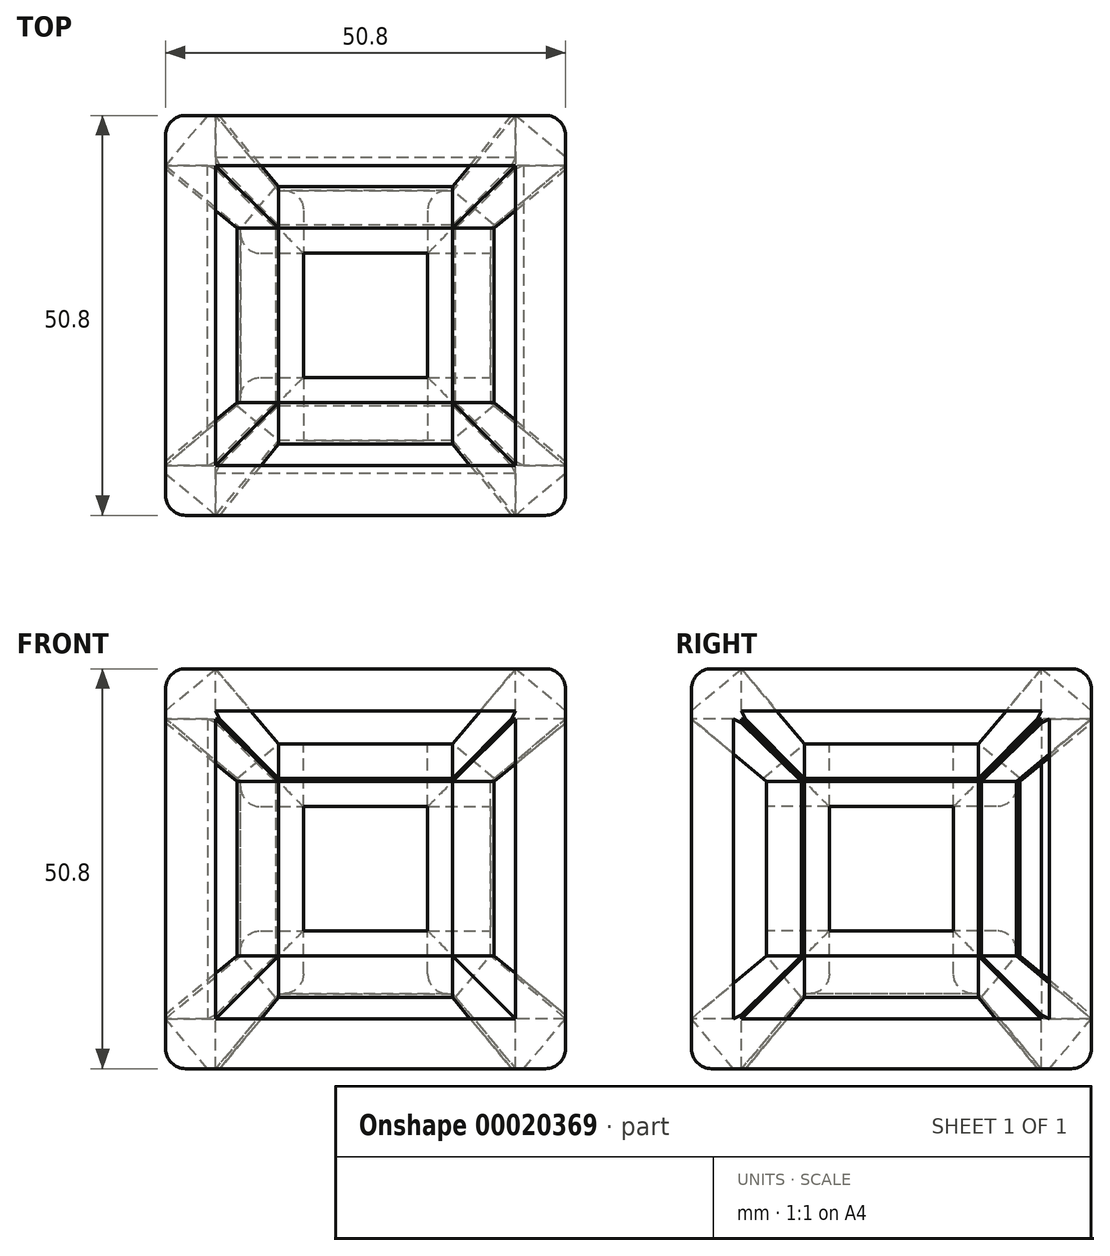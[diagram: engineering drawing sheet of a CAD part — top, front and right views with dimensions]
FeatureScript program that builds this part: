
annotation { "Feature Type Name" : "Feature", "Feature Type Description" : "" }
export const myFeature = defineFeature(function(context is Context, id is Id, definition is map)
    precondition{}
    {
        {
            var Q0;
            Q0=qCreatedBy(makeId("Front.planeOp"),FACE);
            var sketch = newSketch(context, id + "F0", { "sketchPlane" : qUnion([Q0])});
            skLineSegment(sketch, "E0.rect.bottom", {"start": v(-50.8, 50.8) * mm, "end": v(50.8, 50.8) * mm});
            skLineSegment(sketch, "E0.rect.top", {"start": v(-50.8, -50.8) * mm, "end": v(50.8, -50.8) * mm});
            skLineSegment(sketch, "E0.rect.left", {"start": v(-50.8, 50.8) * mm, "end": v(-50.8, -50.8) * mm});
            skLineSegment(sketch, "E0.rect.right", {"start": v(50.8, 50.8) * mm, "end": v(50.8, -50.8) * mm});
            skPoint(sketch, "E0.rect.middle", {"position": v(0, 0) * mm});
            skLineSegment(sketch, "E1.rect.bottom", {"start": v(-44.45, 44.45) * mm, "end": v(44.45, 44.45) * mm});
            skLineSegment(sketch, "E1.rect.top", {"start": v(-44.45, -44.45) * mm, "end": v(44.45, -44.45) * mm});
            skLineSegment(sketch, "E1.rect.left", {"start": v(-44.45, 44.45) * mm, "end": v(-44.45, -44.45) * mm});
            skLineSegment(sketch, "E1.rect.right", {"start": v(44.45, 44.45) * mm, "end": v(44.45, -44.45) * mm});
            skSolve(sketch);
        }
        {
            var Q0;
            Q0=makeQuery(id+"F0.imprint","IMPRINT",FACE,{"disambiguationData":[TD([[makeQuery(id+"F0.imprint","IMPRINT",EDGE,{"derivedFrom":sQuery(id+"F0.wireOp",EDGE,"E0.rect.bottom")}),-1.0]])]});
            var Q1;
            Q1=makeQuery(id+"F0.imprint","IMPRINT",FACE,{"disambiguationData":[TD([[makeQuery(id+"F0.imprint","IMPRINT",EDGE,{"derivedFrom":sQuery(id+"F0.wireOp",EDGE,"E1.rect.bottom")}),-1.0]])]});
            extrude(context, id + "F1", {"entities" : qUnion([Q0, Q1]), "oppositeDirection" : true, "depth" : 101.6 * mm});
        }
        {
            var Q0;
            Q0=makeQuery(id+"F1.opExtrude","CAP_FACE",FACE,{"disambiguationData":[OSD([sQuery(id+"F0.wireOp",EDGE,"E0.rect.bottom"),sQuery(id+"F0.wireOp",EDGE,"E0.rect.top"),sQuery(id+"F0.wireOp",EDGE,"E0.rect.left"),sQuery(id+"F0.wireOp",EDGE,"E0.rect.right")])],"isStart":true});
            var sketch = newSketch(context, id + "F2", { "sketchPlane" : qUnion([Q0])});
            skLineSegment(sketch, "E2.rect.bottom", {"start": v(-38.1, 38.1) * mm, "end": v(38.1, 38.1) * mm});
            skLineSegment(sketch, "E2.rect.top", {"start": v(-38.1, -38.1) * mm, "end": v(38.1, -38.1) * mm});
            skLineSegment(sketch, "E2.rect.left", {"start": v(-38.1, 38.1) * mm, "end": v(-38.1, -38.1) * mm});
            skLineSegment(sketch, "E2.rect.right", {"start": v(38.1, 38.1) * mm, "end": v(38.1, -38.1) * mm});
            skPoint(sketch, "E2.rect.middle", {"position": v(0, 0) * mm});
            skSolve(sketch);
        }
        {
            var Q0;
            Q0=makeQuery(id+"F2.imprint","IMPRINT",FACE,{"disambiguationData":[TD([[makeQuery(id+"F2.imprint","IMPRINT",EDGE,{"derivedFrom":sQuery(id+"F2.wireOp",EDGE,"E2.rect.bottom")}),-1.0]])]});
            extrude(context, id + "F3", {"entities" : qUnion([Q0]), "operationType" : NewBodyOperationType.REMOVE, "oppositeDirection" : true, "depth" : 19.05 * mm, "hasDraft" : true, "draftAngle" : 40 * degree, "draftPullDirection" : true});
        }
        {
            var Q0;
            Q0=makeQuery(id+"F1.opExtrude","SWEPT_FACE",FACE,{"disambiguationData":[OSD([sQuery(id+"F0.wireOp",EDGE,"E0.rect.right")])]});
            var sketch = newSketch(context, id + "F4", { "sketchPlane" : qUnion([Q0])});
            skLineSegment(sketch, "E3.rect.bottom", {"start": v(12.7, 38.1) * mm, "end": v(88.9, 38.1) * mm});
            skLineSegment(sketch, "E3.rect.top", {"start": v(12.7, -38.1) * mm, "end": v(88.9, -38.1) * mm});
            skLineSegment(sketch, "E3.rect.left", {"start": v(12.7, 38.1) * mm, "end": v(12.7, -38.1) * mm});
            skLineSegment(sketch, "E3.rect.right", {"start": v(88.9, 38.1) * mm, "end": v(88.9, -38.1) * mm});
            skPoint(sketch, "E3.rect.middle", {"position": v(50.8, 0) * mm});
            skPoint(sketch, "E4.start.orphan", {"position": v(0, 50.8) * mm});
            skPoint(sketch, "E5.trimOffspring.end.orphan", {"position": v(101.6, -50.8) * mm});
            skSolve(sketch);
        }
        {
            var Q0;
            Q0=makeQuery(id+"F4.imprint","IMPRINT",FACE,{"disambiguationData":[TD([[makeQuery(id+"F4.imprint","IMPRINT",EDGE,{"derivedFrom":sQuery(id+"F4.wireOp",EDGE,"E3.rect.bottom")}),-1.0]])]});
            extrude(context, id + "F5", {"entities" : qUnion([Q0]), "operationType" : NewBodyOperationType.REMOVE, "oppositeDirection" : true, "depth" : 19.05 * mm, "hasDraft" : true, "draftAngle" : 40 * degree, "draftPullDirection" : true});
        }
        {
            var Q0;
            Q0=makeQuery(id+"F1.opExtrude","CAP_FACE",FACE,{"disambiguationData":[OSD([sQuery(id+"F0.wireOp",EDGE,"E0.rect.bottom"),sQuery(id+"F0.wireOp",EDGE,"E0.rect.top"),sQuery(id+"F0.wireOp",EDGE,"E0.rect.left"),sQuery(id+"F0.wireOp",EDGE,"E0.rect.right")])],"isStart":false});
            var sketch = newSketch(context, id + "F6", { "sketchPlane" : qUnion([Q0])});
            skLineSegment(sketch, "E6.rect.bottom", {"start": v(-38.1, 38.1) * mm, "end": v(38.1, 38.1) * mm});
            skLineSegment(sketch, "E6.rect.top", {"start": v(-38.1, -38.1) * mm, "end": v(38.1, -38.1) * mm});
            skLineSegment(sketch, "E6.rect.left", {"start": v(-38.1, 38.1) * mm, "end": v(-38.1, -38.1) * mm});
            skLineSegment(sketch, "E6.rect.right", {"start": v(38.1, 38.1) * mm, "end": v(38.1, -38.1) * mm});
            skPoint(sketch, "E6.rect.middle", {"position": v(0, 0) * mm});
            skPoint(sketch, "E7.trimOffspring.end.orphan", {"position": v(50.8, -50.8) * mm});
            skPoint(sketch, "E8.start.orphan", {"position": v(-50.8, 50.8) * mm});
            skSolve(sketch);
        }
        {
            var Q0;
            Q0=makeQuery(id+"F6.imprint","IMPRINT",FACE,{"disambiguationData":[TD([[makeQuery(id+"F6.imprint","IMPRINT",EDGE,{"derivedFrom":sQuery(id+"F6.wireOp",EDGE,"E6.rect.bottom")}),-1.0]])]});
            extrude(context, id + "F7", {"entities" : qUnion([Q0]), "operationType" : NewBodyOperationType.REMOVE, "oppositeDirection" : true, "depth" : 19.05 * mm, "hasDraft" : true, "draftAngle" : 40 * degree, "draftPullDirection" : true});
        }
        {
            var Q0;
            Q0=makeQuery(id+"F1.opExtrude","SWEPT_FACE",FACE,{"disambiguationData":[OSD([sQuery(id+"F0.wireOp",EDGE,"E0.rect.left")])]});
            var sketch = newSketch(context, id + "F8", { "sketchPlane" : qUnion([Q0])});
            skLineSegment(sketch, "E9.rect.bottom", {"start": v(-88.9, 38.1) * mm, "end": v(-12.7, 38.1) * mm});
            skLineSegment(sketch, "E9.rect.top", {"start": v(-88.9, -38.1) * mm, "end": v(-12.7, -38.1) * mm});
            skLineSegment(sketch, "E9.rect.left", {"start": v(-88.9, 38.1) * mm, "end": v(-88.9, -38.1) * mm});
            skLineSegment(sketch, "E9.rect.right", {"start": v(-12.7, 38.1) * mm, "end": v(-12.7, -38.1) * mm});
            skPoint(sketch, "E9.rect.middle", {"position": v(-50.8, 0) * mm});
            skPoint(sketch, "E10.trimOffspring.end.orphan", {"position": v(-101.6, -50.8) * mm});
            skPoint(sketch, "E11.start.orphan", {"position": v(0, 50.8) * mm});
            skSolve(sketch);
        }
        {
            var Q0;
            Q0=makeQuery(id+"F8.imprint","IMPRINT",FACE,{"disambiguationData":[TD([[makeQuery(id+"F8.imprint","IMPRINT",EDGE,{"derivedFrom":sQuery(id+"F8.wireOp",EDGE,"E9.rect.bottom")}),-1.0]])]});
            extrude(context, id + "F9", {"entities" : qUnion([Q0]), "operationType" : NewBodyOperationType.REMOVE, "oppositeDirection" : true, "depth" : 19.05 * mm, "hasDraft" : true, "draftAngle" : 40 * degree, "draftPullDirection" : true});
        }
        {
            var Q0;
            Q0=makeQuery(id+"F1.opExtrude","SWEPT_FACE",FACE,{"disambiguationData":[OSD([sQuery(id+"F0.wireOp",EDGE,"E0.rect.bottom")])]});
            var sketch = newSketch(context, id + "F10", { "sketchPlane" : qUnion([Q0])});
            skLineSegment(sketch, "E12.rect.bottom", {"start": v(-38.1, 12.7) * mm, "end": v(38.1, 12.7) * mm});
            skLineSegment(sketch, "E12.rect.top", {"start": v(-38.1, 88.9) * mm, "end": v(38.1, 88.9) * mm});
            skLineSegment(sketch, "E12.rect.left", {"start": v(-38.1, 12.7) * mm, "end": v(-38.1, 88.9) * mm});
            skLineSegment(sketch, "E12.rect.right", {"start": v(38.1, 12.7) * mm, "end": v(38.1, 88.9) * mm});
            skPoint(sketch, "E12.rect.middle", {"position": v(0, 50.8) * mm});
            skPoint(sketch, "E13.orphan", {"position": v(50.8, 101.6) * mm});
            skPoint(sketch, "E14.orphan", {"position": v(-50.8, 0) * mm});
            skSolve(sketch);
        }
        {
            var Q0;
            Q0=makeQuery(id+"F10.imprint","IMPRINT",FACE,{"disambiguationData":[TD([[makeQuery(id+"F10.imprint","IMPRINT",EDGE,{"derivedFrom":sQuery(id+"F10.wireOp",EDGE,"E12.rect.bottom")}),1.0]])]});
            extrude(context, id + "F11", {"entities" : qUnion([Q0]), "operationType" : NewBodyOperationType.REMOVE, "oppositeDirection" : true, "depth" : 19.05 * mm, "hasDraft" : true, "draftAngle" : 40 * degree, "draftPullDirection" : true});
        }
        {
            var Q0;
            Q0=makeQuery(id+"F1.opExtrude","SWEPT_FACE",FACE,{"disambiguationData":[OSD([sQuery(id+"F0.wireOp",EDGE,"E0.rect.top")])]});
            var sketch = newSketch(context, id + "F12", { "sketchPlane" : qUnion([Q0])});
            skLineSegment(sketch, "E15.rect.bottom", {"start": v(-38.1, -12.7) * mm, "end": v(38.1, -12.7) * mm});
            skLineSegment(sketch, "E15.rect.top", {"start": v(-38.1, -88.9) * mm, "end": v(38.1, -88.9) * mm});
            skLineSegment(sketch, "E15.rect.left", {"start": v(-38.1, -12.7) * mm, "end": v(-38.1, -88.9) * mm});
            skLineSegment(sketch, "E15.rect.right", {"start": v(38.1, -12.7) * mm, "end": v(38.1, -88.9) * mm});
            skPoint(sketch, "E15.rect.middle", {"position": v(0, -50.8) * mm});
            skPoint(sketch, "E16.trimOffspring.end.orphan", {"position": v(50.8, -101.6) * mm});
            skPoint(sketch, "E17.start.orphan", {"position": v(-50.8, 0) * mm});
            skSolve(sketch);
        }
        {
            var Q0;
            Q0=makeQuery(id+"F12.imprint","IMPRINT",FACE,{"disambiguationData":[TD([[makeQuery(id+"F12.imprint","IMPRINT",EDGE,{"derivedFrom":sQuery(id+"F12.wireOp",EDGE,"E15.rect.bottom")}),-1.0]])]});
            extrude(context, id + "F13", {"entities" : qUnion([Q0]), "operationType" : NewBodyOperationType.REMOVE, "oppositeDirection" : true, "depth" : 19.05 * mm, "hasDraft" : true, "draftAngle" : 40 * degree, "draftPullDirection" : true});
        }
        {
            var Q0;
            Q0=makeQuery(id+"F3.boolean.opBoolean","COPY",FACE,{"derivedFrom":makeQuery(id+"F3.opExtrude","CAP_FACE",FACE,{"disambiguationData":[OSD([sQuery(id+"F2.wireOp",EDGE,"E2.rect.bottom"),sQuery(id+"F2.wireOp",EDGE,"E2.rect.top"),sQuery(id+"F2.wireOp",EDGE,"E2.rect.left"),sQuery(id+"F2.wireOp",EDGE,"E2.rect.right")])],"isStart":false})});
            var sketch = newSketch(context, id + "F14", { "sketchPlane" : qUnion([Q0])});
            skLineSegment(sketch, "E18.0", {"start": v(-15.77, 15.77) * mm, "end": v(15.77, 15.77) * mm});
            skLineSegment(sketch, "E18.1", {"start": v(-15.77, 15.77) * mm, "end": v(-15.77, -15.77) * mm});
            skLineSegment(sketch, "E18.2", {"start": v(-15.77, -15.77) * mm, "end": v(15.77, -15.77) * mm});
            skLineSegment(sketch, "E18.3", {"start": v(15.77, 15.77) * mm, "end": v(15.77, -15.77) * mm});
            skSolve(sketch);
        }
        {
            var Q0;
            Q0=makeQuery(id+"F14.imprint","IMPRINT",FACE,{"disambiguationData":[TD([[makeQuery(id+"F14.imprint","IMPRINT",EDGE,{"derivedFrom":sQuery(id+"F14.wireOp",EDGE,"E18.0")}),-1.0]])]});
            extrude(context, id + "F15", {"entities" : qUnion([Q0]), "operationType" : NewBodyOperationType.REMOVE, "endBound" : BoundingType.THROUGH_ALL, "oppositeDirection" : true, "depth" : 25.4 * mm});
        }
        {
            var Q0;
            Q0=makeQuery(id+"F11.boolean.opBoolean","COPY",FACE,{"derivedFrom":makeQuery(id+"F11.opExtrude","CAP_FACE",FACE,{"disambiguationData":[OSD([sQuery(id+"F10.wireOp",EDGE,"E12.rect.bottom"),sQuery(id+"F10.wireOp",EDGE,"E12.rect.top"),sQuery(id+"F10.wireOp",EDGE,"E12.rect.left"),sQuery(id+"F10.wireOp",EDGE,"E12.rect.right")])],"isStart":false})});
            var sketch = newSketch(context, id + "F16", { "sketchPlane" : qUnion([Q0])});
            skLineSegment(sketch, "E19.0", {"start": v(-15.77, 35.03) * mm, "end": v(-15.77, 66.57) * mm});
            skLineSegment(sketch, "E19.1", {"start": v(-15.77, 35.03) * mm, "end": v(15.77, 35.03) * mm});
            skLineSegment(sketch, "E19.2", {"start": v(15.77, 35.03) * mm, "end": v(15.77, 66.57) * mm});
            skLineSegment(sketch, "E19.3", {"start": v(-15.77, 66.57) * mm, "end": v(15.77, 66.57) * mm});
            skSolve(sketch);
        }
        {
            var Q0;
            Q0=makeQuery(id+"F16.imprint","IMPRINT",FACE,{"disambiguationData":[TD([[makeQuery(id+"F16.imprint","IMPRINT",EDGE,{"derivedFrom":sQuery(id+"F16.wireOp",EDGE,"E19.0")}),-1.0]])]});
            extrude(context, id + "F17", {"entities" : qUnion([Q0]), "operationType" : NewBodyOperationType.REMOVE, "endBound" : BoundingType.THROUGH_ALL, "oppositeDirection" : true, "depth" : 25.4 * mm});
        }
        {
            var Q0;
            Q0=makeQuery(id+"F5.boolean.opBoolean","COPY",FACE,{"derivedFrom":makeQuery(id+"F5.opExtrude","CAP_FACE",FACE,{"disambiguationData":[OSD([sQuery(id+"F4.wireOp",EDGE,"E3.rect.bottom"),sQuery(id+"F4.wireOp",EDGE,"E3.rect.top"),sQuery(id+"F4.wireOp",EDGE,"E3.rect.left"),sQuery(id+"F4.wireOp",EDGE,"E3.rect.right")])],"isStart":false})});
            var sketch = newSketch(context, id + "F18", { "sketchPlane" : qUnion([Q0])});
            skLineSegment(sketch, "E20.0", {"start": v(35.03, 15.77) * mm, "end": v(66.57, 15.77) * mm});
            skLineSegment(sketch, "E20.1", {"start": v(35.03, 15.77) * mm, "end": v(35.03, -15.77) * mm});
            skLineSegment(sketch, "E20.2", {"start": v(35.03, -15.77) * mm, "end": v(66.57, -15.77) * mm});
            skLineSegment(sketch, "E20.3", {"start": v(66.57, 15.77) * mm, "end": v(66.57, -15.77) * mm});
            skSolve(sketch);
        }
        {
            var Q0;
            Q0=makeQuery(id+"F18.imprint","IMPRINT",FACE,{"disambiguationData":[TD([[makeQuery(id+"F18.imprint","IMPRINT",EDGE,{"derivedFrom":sQuery(id+"F18.wireOp",EDGE,"E20.0")}),-1.0]])]});
            extrude(context, id + "F19", {"entities" : qUnion([Q0]), "operationType" : NewBodyOperationType.REMOVE, "endBound" : BoundingType.THROUGH_ALL, "oppositeDirection" : true, "depth" : 25.4 * mm});
        }
        {
            var Q0;
            Q0=makeQuery(id+"F11.boolean.opBoolean","COPY",FACE,{"derivedFrom":makeQuery(id+"F11.opExtrude","SWEPT_FACE",FACE,{"disambiguationData":[OSD([sQuery(id+"F10.wireOp",EDGE,"E12.rect.left")])]})});
            extrude(context, id + "F20", {"entities" : qUnion([Q0]), "operationType" : NewBodyOperationType.REMOVE, "oppositeDirection" : true, "depth" : 25.4 * mm});
        }
        {
            var Q0;
            Q0=makeQuery(id+"F11.boolean.opBoolean","COPY",FACE,{"derivedFrom":makeQuery(id+"F11.opExtrude","SWEPT_FACE",FACE,{"disambiguationData":[OSD([sQuery(id+"F10.wireOp",EDGE,"E12.rect.bottom")])]})});
            extrude(context, id + "F21", {"entities" : qUnion([Q0]), "operationType" : NewBodyOperationType.REMOVE, "oppositeDirection" : true, "depth" : 25.4 * mm});
        }
        {
            var Q0;
            Q0=makeQuery(id+"F11.boolean.opBoolean","COPY",FACE,{"derivedFrom":makeQuery(id+"F11.opExtrude","SWEPT_FACE",FACE,{"disambiguationData":[OSD([sQuery(id+"F10.wireOp",EDGE,"E12.rect.top")])]})});
            extrude(context, id + "F22", {"entities" : qUnion([Q0]), "operationType" : NewBodyOperationType.REMOVE, "oppositeDirection" : true, "depth" : 25.4 * mm});
        }
        {
            var Q0;
            Q0=makeQuery(id+"F11.boolean.opBoolean","COPY",FACE,{"derivedFrom":makeQuery(id+"F11.opExtrude","SWEPT_FACE",FACE,{"disambiguationData":[OSD([sQuery(id+"F10.wireOp",EDGE,"E12.rect.right")])]})});
            extrude(context, id + "F23", {"entities" : qUnion([Q0]), "operationType" : NewBodyOperationType.REMOVE, "oppositeDirection" : true, "depth" : 25.4 * mm});
        }
        {
            var Q0;
            Q0=makeQuery(id+"F3.boolean.opBoolean","COPY",FACE,{"derivedFrom":makeQuery(id+"F3.opExtrude","SWEPT_FACE",FACE,{"disambiguationData":[OSD([sQuery(id+"F2.wireOp",EDGE,"E2.rect.left")])]})});
            extrude(context, id + "F24", {"entities" : qUnion([Q0]), "operationType" : NewBodyOperationType.REMOVE, "oppositeDirection" : true, "depth" : 25.4 * mm});
        }
        {
            var Q0;
            Q0=makeQuery(id+"F3.boolean.opBoolean","COPY",FACE,{"derivedFrom":makeQuery(id+"F3.opExtrude","SWEPT_FACE",FACE,{"disambiguationData":[OSD([sQuery(id+"F2.wireOp",EDGE,"E2.rect.top")])]})});
            extrude(context, id + "F25", {"entities" : qUnion([Q0]), "operationType" : NewBodyOperationType.REMOVE, "oppositeDirection" : true, "depth" : 25.4 * mm});
        }
        {
            var Q0;
            Q0=makeQuery(id+"F3.boolean.opBoolean","COPY",FACE,{"derivedFrom":makeQuery(id+"F3.opExtrude","SWEPT_FACE",FACE,{"disambiguationData":[OSD([sQuery(id+"F2.wireOp",EDGE,"E2.rect.right")])]})});
            extrude(context, id + "F26", {"entities" : qUnion([Q0]), "operationType" : NewBodyOperationType.REMOVE, "oppositeDirection" : true, "depth" : 25.4 * mm});
        }
        {
            var Q0;
            Q0=makeQuery(id+"F9.boolean.opBoolean","COPY",FACE,{"derivedFrom":makeQuery(id+"F9.opExtrude","SWEPT_FACE",FACE,{"disambiguationData":[OSD([sQuery(id+"F8.wireOp",EDGE,"E9.rect.top")])]})});
            extrude(context, id + "F27", {"entities" : qUnion([Q0]), "operationType" : NewBodyOperationType.REMOVE, "oppositeDirection" : true, "depth" : 25.4 * mm});
        }
        {
            var Q0;
            Q0=makeQuery(id+"F9.boolean.opBoolean","COPY",FACE,{"derivedFrom":makeQuery(id+"F9.opExtrude","SWEPT_FACE",FACE,{"disambiguationData":[OSD([sQuery(id+"F8.wireOp",EDGE,"E9.rect.left")])]})});
            extrude(context, id + "F28", {"entities" : qUnion([Q0]), "operationType" : NewBodyOperationType.REMOVE, "oppositeDirection" : true, "depth" : 25.4 * mm});
        }
        {
            var Q0;
            Q0=makeQuery(id+"F7.boolean.opBoolean","COPY",FACE,{"derivedFrom":makeQuery(id+"F7.opExtrude","SWEPT_FACE",FACE,{"disambiguationData":[OSD([sQuery(id+"F6.wireOp",EDGE,"E6.rect.left")])]})});
            extrude(context, id + "F29", {"entities" : qUnion([Q0]), "operationType" : NewBodyOperationType.REMOVE, "oppositeDirection" : true, "depth" : 25.4 * mm});
        }
        {
            var Q0;
            Q0=makeQuery(id+"F7.boolean.opBoolean","COPY",FACE,{"derivedFrom":makeQuery(id+"F7.opExtrude","SWEPT_FACE",FACE,{"disambiguationData":[OSD([sQuery(id+"F6.wireOp",EDGE,"E6.rect.top")])]})});
            extrude(context, id + "F30", {"entities" : qUnion([Q0]), "operationType" : NewBodyOperationType.REMOVE, "oppositeDirection" : true, "depth" : 25.4 * mm});
        }
        {
            var Q0;
            Q0=makeQuery(id+"F5.boolean.opBoolean","COPY",FACE,{"derivedFrom":makeQuery(id+"F5.opExtrude","SWEPT_FACE",FACE,{"disambiguationData":[OSD([sQuery(id+"F4.wireOp",EDGE,"E3.rect.top")])]})});
            extrude(context, id + "F31", {"entities" : qUnion([Q0]), "operationType" : NewBodyOperationType.REMOVE, "oppositeDirection" : true, "depth" : 25.4 * mm});
        }
        {
            var Q0;
            Q0=makeQuery(id+"F1.opExtrude","CAP_EDGE",EDGE,{"disambiguationData":[OSD([sQuery(id+"F0.wireOp",EDGE,"E0.rect.bottom")])],"isStart":false});
            var Q1;
            Q1=makeQuery(id+"F1.opExtrude","CAP_EDGE",EDGE,{"disambiguationData":[OSD([sQuery(id+"F0.wireOp",EDGE,"E0.rect.left")])],"isStart":false});
            var Q2;
            Q2=makeQuery(id+"F1.opExtrude","SWEPT_EDGE",EDGE,{"disambiguationData":[OSD([sQuery(id+"F0.wireOp",EDGE,"E0.rect.bottom"),sQuery(id+"F0.wireOp",EDGE,"E0.rect.left")])]});
            var Q3;
            Q3=makeQuery(id+"F1.opExtrude","CAP_EDGE",EDGE,{"disambiguationData":[OSD([sQuery(id+"F0.wireOp",EDGE,"E0.rect.right")])],"isStart":false});
            var Q4;
            Q4=makeQuery(id+"F1.opExtrude","CAP_EDGE",EDGE,{"disambiguationData":[OSD([sQuery(id+"F0.wireOp",EDGE,"E0.rect.top")])],"isStart":false});
            var Q5;
            Q5=makeQuery(id+"F1.opExtrude","SWEPT_EDGE",EDGE,{"disambiguationData":[OSD([sQuery(id+"F0.wireOp",EDGE,"E0.rect.top"),sQuery(id+"F0.wireOp",EDGE,"E0.rect.left")])]});
            var Q6;
            Q6=makeQuery(id+"F1.opExtrude","CAP_EDGE",EDGE,{"disambiguationData":[OSD([sQuery(id+"F0.wireOp",EDGE,"E0.rect.left")])],"isStart":true});
            var Q7;
            Q7=makeQuery(id+"F1.opExtrude","CAP_EDGE",EDGE,{"disambiguationData":[OSD([sQuery(id+"F0.wireOp",EDGE,"E0.rect.bottom")])],"isStart":true});
            var Q8;
            Q8=makeQuery(id+"F1.opExtrude","SWEPT_EDGE",EDGE,{"disambiguationData":[OSD([sQuery(id+"F0.wireOp",EDGE,"E0.rect.bottom"),sQuery(id+"F0.wireOp",EDGE,"E0.rect.right")])]});
            var Q9;
            Q9=makeQuery(id+"F1.opExtrude","CAP_EDGE",EDGE,{"disambiguationData":[OSD([sQuery(id+"F0.wireOp",EDGE,"E0.rect.right")])],"isStart":true});
            var Q10;
            Q10=makeQuery(id+"F1.opExtrude","SWEPT_EDGE",EDGE,{"disambiguationData":[OSD([sQuery(id+"F0.wireOp",EDGE,"E0.rect.top"),sQuery(id+"F0.wireOp",EDGE,"E0.rect.right")])]});
            var Q11;
            Q11=makeQuery(id+"F1.opExtrude","CAP_EDGE",EDGE,{"disambiguationData":[OSD([sQuery(id+"F0.wireOp",EDGE,"E0.rect.top")])],"isStart":true});
            fillet(context, id + "F32", {"entities" : qUnion([Q0, Q1, Q2, Q3, Q4, Q5, Q6, Q7, Q8, Q9, Q10, Q11]), "radius" : 5.08 * mm, "tangentPropagation" : true, "allowEdgeOverflow" : false});
        }
        {
            var Q0;
            Q0=makeQuery(id+"F15.boolean.opBoolean","COPY",EDGE,{"derivedFrom":makeQuery(id+"F15.opExtrude","CAP_EDGE",EDGE,{"disambiguationData":[OSD([sQuery(id+"F14.wireOp",EDGE,"E18.1")])],"isStart":true})});
            var Q1;
            Q1=makeQuery(id+"F15.boolean.opBoolean","COPY",EDGE,{"derivedFrom":makeQuery(id+"F15.opExtrude","CAP_EDGE",EDGE,{"disambiguationData":[OSD([sQuery(id+"F14.wireOp",EDGE,"E18.0")])],"isStart":true})});
            var Q2;
            Q2=makeQuery(id+"F15.boolean.opBoolean","COPY",EDGE,{"derivedFrom":makeQuery(id+"F15.opExtrude","CAP_EDGE",EDGE,{"disambiguationData":[OSD([sQuery(id+"F14.wireOp",EDGE,"E18.3")])],"isStart":true})});
            var Q3;
            Q3=makeQuery(id+"F15.boolean.opBoolean","COPY",EDGE,{"derivedFrom":makeQuery(id+"F15.opExtrude","CAP_EDGE",EDGE,{"disambiguationData":[OSD([sQuery(id+"F14.wireOp",EDGE,"E18.2")])],"isStart":true})});
            var Q4;
            Q4=makeQuery(id+"F19.boolean.opBoolean","COPY",EDGE,{"derivedFrom":makeQuery(id+"F19.opExtrude","CAP_EDGE",EDGE,{"disambiguationData":[OSD([sQuery(id+"F18.wireOp",EDGE,"E20.1")])],"isStart":true})});
            var Q5;
            Q5=makeQuery(id+"F19.boolean.opBoolean","COPY",EDGE,{"derivedFrom":makeQuery(id+"F19.opExtrude","CAP_EDGE",EDGE,{"disambiguationData":[OSD([sQuery(id+"F18.wireOp",EDGE,"E20.0")])],"isStart":true})});
            var Q6;
            Q6=makeQuery(id+"F19.boolean.opBoolean","COPY",EDGE,{"derivedFrom":makeQuery(id+"F19.opExtrude","CAP_EDGE",EDGE,{"disambiguationData":[OSD([sQuery(id+"F18.wireOp",EDGE,"E20.2")])],"isStart":true})});
            var Q7;
            Q7=makeQuery(id+"F19.boolean.opBoolean","COPY",EDGE,{"derivedFrom":makeQuery(id+"F19.opExtrude","CAP_EDGE",EDGE,{"disambiguationData":[OSD([sQuery(id+"F18.wireOp",EDGE,"E20.3")])],"isStart":true})});
            var Q8;
            Q8=makeQuery(id+"F15.boolean.opBoolean","INTERSECT",EDGE,{"derivedFrom":[makeQuery(id+"F7.boolean.opBoolean","COPY",FACE,{"derivedFrom":makeQuery(id+"F7.opExtrude","CAP_FACE",FACE,{"disambiguationData":[OSD([sQuery(id+"F6.wireOp",EDGE,"E6.rect.bottom"),sQuery(id+"F6.wireOp",EDGE,"E6.rect.top"),sQuery(id+"F6.wireOp",EDGE,"E6.rect.left"),sQuery(id+"F6.wireOp",EDGE,"E6.rect.right")])],"isStart":false})}),makeQuery(id+"F15.opExtrude","SWEPT_FACE",FACE,{"disambiguationData":[OSD([sQuery(id+"F14.wireOp",EDGE,"E18.2")])]})]});
            var Q9;
            Q9=makeQuery(id+"F15.boolean.opBoolean","INTERSECT",EDGE,{"derivedFrom":[makeQuery(id+"F7.boolean.opBoolean","COPY",FACE,{"derivedFrom":makeQuery(id+"F7.opExtrude","CAP_FACE",FACE,{"disambiguationData":[OSD([sQuery(id+"F6.wireOp",EDGE,"E6.rect.bottom"),sQuery(id+"F6.wireOp",EDGE,"E6.rect.top"),sQuery(id+"F6.wireOp",EDGE,"E6.rect.left"),sQuery(id+"F6.wireOp",EDGE,"E6.rect.right")])],"isStart":false})}),makeQuery(id+"F15.opExtrude","SWEPT_FACE",FACE,{"disambiguationData":[OSD([sQuery(id+"F14.wireOp",EDGE,"E18.1")])]})]});
            var Q10;
            Q10=makeQuery(id+"F15.boolean.opBoolean","INTERSECT",EDGE,{"derivedFrom":[makeQuery(id+"F7.boolean.opBoolean","COPY",FACE,{"derivedFrom":makeQuery(id+"F7.opExtrude","CAP_FACE",FACE,{"disambiguationData":[OSD([sQuery(id+"F6.wireOp",EDGE,"E6.rect.bottom"),sQuery(id+"F6.wireOp",EDGE,"E6.rect.top"),sQuery(id+"F6.wireOp",EDGE,"E6.rect.left"),sQuery(id+"F6.wireOp",EDGE,"E6.rect.right")])],"isStart":false})}),makeQuery(id+"F15.opExtrude","SWEPT_FACE",FACE,{"disambiguationData":[OSD([sQuery(id+"F14.wireOp",EDGE,"E18.0")])]})]});
            var Q11;
            Q11=makeQuery(id+"F15.boolean.opBoolean","INTERSECT",EDGE,{"derivedFrom":[makeQuery(id+"F7.boolean.opBoolean","COPY",FACE,{"derivedFrom":makeQuery(id+"F7.opExtrude","CAP_FACE",FACE,{"disambiguationData":[OSD([sQuery(id+"F6.wireOp",EDGE,"E6.rect.bottom"),sQuery(id+"F6.wireOp",EDGE,"E6.rect.top"),sQuery(id+"F6.wireOp",EDGE,"E6.rect.left"),sQuery(id+"F6.wireOp",EDGE,"E6.rect.right")])],"isStart":false})}),makeQuery(id+"F15.opExtrude","SWEPT_FACE",FACE,{"disambiguationData":[OSD([sQuery(id+"F14.wireOp",EDGE,"E18.3")])]})]});
            var Q12;
            Q12=makeQuery(id+"F19.boolean.opBoolean","INTERSECT",EDGE,{"derivedFrom":[makeQuery(id+"F9.boolean.opBoolean","COPY",FACE,{"derivedFrom":makeQuery(id+"F9.opExtrude","CAP_FACE",FACE,{"disambiguationData":[OSD([sQuery(id+"F8.wireOp",EDGE,"E9.rect.bottom"),sQuery(id+"F8.wireOp",EDGE,"E9.rect.top"),sQuery(id+"F8.wireOp",EDGE,"E9.rect.left"),sQuery(id+"F8.wireOp",EDGE,"E9.rect.right")])],"isStart":false})}),makeQuery(id+"F19.opExtrude","SWEPT_FACE",FACE,{"disambiguationData":[OSD([sQuery(id+"F18.wireOp",EDGE,"E20.3")])]})]});
            var Q13;
            Q13=makeQuery(id+"F19.boolean.opBoolean","INTERSECT",EDGE,{"derivedFrom":[makeQuery(id+"F9.boolean.opBoolean","COPY",FACE,{"derivedFrom":makeQuery(id+"F9.opExtrude","CAP_FACE",FACE,{"disambiguationData":[OSD([sQuery(id+"F8.wireOp",EDGE,"E9.rect.bottom"),sQuery(id+"F8.wireOp",EDGE,"E9.rect.top"),sQuery(id+"F8.wireOp",EDGE,"E9.rect.left"),sQuery(id+"F8.wireOp",EDGE,"E9.rect.right")])],"isStart":false})}),makeQuery(id+"F19.opExtrude","SWEPT_FACE",FACE,{"disambiguationData":[OSD([sQuery(id+"F18.wireOp",EDGE,"E20.0")])]})]});
            var Q14;
            Q14=makeQuery(id+"F19.boolean.opBoolean","INTERSECT",EDGE,{"derivedFrom":[makeQuery(id+"F9.boolean.opBoolean","COPY",FACE,{"derivedFrom":makeQuery(id+"F9.opExtrude","CAP_FACE",FACE,{"disambiguationData":[OSD([sQuery(id+"F8.wireOp",EDGE,"E9.rect.bottom"),sQuery(id+"F8.wireOp",EDGE,"E9.rect.top"),sQuery(id+"F8.wireOp",EDGE,"E9.rect.left"),sQuery(id+"F8.wireOp",EDGE,"E9.rect.right")])],"isStart":false})}),makeQuery(id+"F19.opExtrude","SWEPT_FACE",FACE,{"disambiguationData":[OSD([sQuery(id+"F18.wireOp",EDGE,"E20.1")])]})]});
            var Q15;
            Q15=makeQuery(id+"F19.boolean.opBoolean","INTERSECT",EDGE,{"derivedFrom":[makeQuery(id+"F9.boolean.opBoolean","COPY",FACE,{"derivedFrom":makeQuery(id+"F9.opExtrude","CAP_FACE",FACE,{"disambiguationData":[OSD([sQuery(id+"F8.wireOp",EDGE,"E9.rect.bottom"),sQuery(id+"F8.wireOp",EDGE,"E9.rect.top"),sQuery(id+"F8.wireOp",EDGE,"E9.rect.left"),sQuery(id+"F8.wireOp",EDGE,"E9.rect.right")])],"isStart":false})}),makeQuery(id+"F19.opExtrude","SWEPT_FACE",FACE,{"disambiguationData":[OSD([sQuery(id+"F18.wireOp",EDGE,"E20.2")])]})]});
            var Q16;
            Q16=makeQuery(id+"F17.boolean.opBoolean","INTERSECT",EDGE,{"derivedFrom":[makeQuery(id+"F13.boolean.opBoolean","COPY",FACE,{"derivedFrom":makeQuery(id+"F13.opExtrude","CAP_FACE",FACE,{"disambiguationData":[OSD([sQuery(id+"F12.wireOp",EDGE,"E15.rect.bottom"),sQuery(id+"F12.wireOp",EDGE,"E15.rect.top"),sQuery(id+"F12.wireOp",EDGE,"E15.rect.left"),sQuery(id+"F12.wireOp",EDGE,"E15.rect.right")])],"isStart":false})}),makeQuery(id+"F17.opExtrude","SWEPT_FACE",FACE,{"disambiguationData":[OSD([sQuery(id+"F16.wireOp",EDGE,"E19.1")])]})]});
            var Q17;
            Q17=makeQuery(id+"F17.boolean.opBoolean","INTERSECT",EDGE,{"derivedFrom":[makeQuery(id+"F13.boolean.opBoolean","COPY",FACE,{"derivedFrom":makeQuery(id+"F13.opExtrude","CAP_FACE",FACE,{"disambiguationData":[OSD([sQuery(id+"F12.wireOp",EDGE,"E15.rect.bottom"),sQuery(id+"F12.wireOp",EDGE,"E15.rect.top"),sQuery(id+"F12.wireOp",EDGE,"E15.rect.left"),sQuery(id+"F12.wireOp",EDGE,"E15.rect.right")])],"isStart":false})}),makeQuery(id+"F17.opExtrude","SWEPT_FACE",FACE,{"disambiguationData":[OSD([sQuery(id+"F16.wireOp",EDGE,"E19.0")])]})]});
            var Q18;
            Q18=makeQuery(id+"F17.boolean.opBoolean","INTERSECT",EDGE,{"derivedFrom":[makeQuery(id+"F13.boolean.opBoolean","COPY",FACE,{"derivedFrom":makeQuery(id+"F13.opExtrude","CAP_FACE",FACE,{"disambiguationData":[OSD([sQuery(id+"F12.wireOp",EDGE,"E15.rect.bottom"),sQuery(id+"F12.wireOp",EDGE,"E15.rect.top"),sQuery(id+"F12.wireOp",EDGE,"E15.rect.left"),sQuery(id+"F12.wireOp",EDGE,"E15.rect.right")])],"isStart":false})}),makeQuery(id+"F17.opExtrude","SWEPT_FACE",FACE,{"disambiguationData":[OSD([sQuery(id+"F16.wireOp",EDGE,"E19.3")])]})]});
            var Q19;
            Q19=makeQuery(id+"F17.boolean.opBoolean","INTERSECT",EDGE,{"derivedFrom":[makeQuery(id+"F13.boolean.opBoolean","COPY",FACE,{"derivedFrom":makeQuery(id+"F13.opExtrude","CAP_FACE",FACE,{"disambiguationData":[OSD([sQuery(id+"F12.wireOp",EDGE,"E15.rect.bottom"),sQuery(id+"F12.wireOp",EDGE,"E15.rect.top"),sQuery(id+"F12.wireOp",EDGE,"E15.rect.left"),sQuery(id+"F12.wireOp",EDGE,"E15.rect.right")])],"isStart":false})}),makeQuery(id+"F17.opExtrude","SWEPT_FACE",FACE,{"disambiguationData":[OSD([sQuery(id+"F16.wireOp",EDGE,"E19.2")])]})]});
            var Q20;
            Q20=makeQuery(id+"F17.boolean.opBoolean","COPY",EDGE,{"derivedFrom":makeQuery(id+"F17.opExtrude","CAP_EDGE",EDGE,{"disambiguationData":[OSD([sQuery(id+"F16.wireOp",EDGE,"E19.0")])],"isStart":true})});
            var Q21;
            Q21=makeQuery(id+"F17.boolean.opBoolean","COPY",EDGE,{"derivedFrom":makeQuery(id+"F17.opExtrude","CAP_EDGE",EDGE,{"disambiguationData":[OSD([sQuery(id+"F16.wireOp",EDGE,"E19.1")])],"isStart":true})});
            var Q22;
            Q22=makeQuery(id+"F17.boolean.opBoolean","COPY",EDGE,{"derivedFrom":makeQuery(id+"F17.opExtrude","CAP_EDGE",EDGE,{"disambiguationData":[OSD([sQuery(id+"F16.wireOp",EDGE,"E19.2")])],"isStart":true})});
            var Q23;
            Q23=makeQuery(id+"F17.boolean.opBoolean","COPY",EDGE,{"derivedFrom":makeQuery(id+"F17.opExtrude","CAP_EDGE",EDGE,{"disambiguationData":[OSD([sQuery(id+"F16.wireOp",EDGE,"E19.3")])],"isStart":true})});
            fillet(context, id + "F33", {"entities" : qUnion([Q0, Q1, Q2, Q3, Q4, Q5, Q6, Q7, Q8, Q9, Q10, Q11, Q12, Q13, Q14, Q15, Q16, Q17, Q18, Q19, Q20, Q21, Q22, Q23]), "radius" : 5.08 * mm, "tangentPropagation" : true, "allowEdgeOverflow" : false});
        }
        {
            var Q0;
            Q0=makeQuery(id+"F1.opExtrude","SWEPT_BODY",BODY,{"disambiguationData":[OSD([sQuery(id+"F0.wireOp",EDGE,"E0.rect.bottom"),sQuery(id+"F0.wireOp",EDGE,"E0.rect.top"),sQuery(id+"F0.wireOp",EDGE,"E0.rect.left"),sQuery(id+"F0.wireOp",EDGE,"E0.rect.right")])]});
            var Q1;
            {var subQ0=sQuery(id+"F0.wireOp",EDGE,"E0.rect.top");var subQ1=sQuery(id+"F0.wireOp",EDGE,"E0.rect.left");Q1=makeQuery(id+"F32.opFillet","BLEND_VERTEX",VERTEX,{"blendedFrom":[makeQuery(id+"F1.opExtrude","CAP_VERTEX",VERTEX,{"disambiguationData":[OSD([subQ0,subQ1])],"isStart":true}),makeQuery(id+"F1.opExtrude","CAP_EDGE",EDGE,{"disambiguationData":[OSD([subQ0])],"isStart":true}),makeQuery(id+"F1.opExtrude","CAP_EDGE",EDGE,{"disambiguationData":[OSD([subQ1])],"isStart":true}),makeQuery(id+"F1.opExtrude","CAP_FACE",FACE,{"disambiguationData":[OSD([sQuery(id+"F0.wireOp",EDGE,"E0.rect.bottom"),subQ0,subQ1,sQuery(id+"F0.wireOp",EDGE,"E0.rect.right")])],"isStart":true})],"blendedInto":[makeQuery(id+"F1.opExtrude","CAP_FACE",FACE,{"disambiguationData":[OSD([sQuery(id+"F0.wireOp",EDGE,"E0.rect.bottom"),subQ0,subQ1,sQuery(id+"F0.wireOp",EDGE,"E0.rect.right")])],"isStart":true})]});}
            transform(context, id + "F34", {"entities" : qUnion([Q0]), "transformType" : TransformType.SCALE_UNIFORMLY, "scale" : 1 / 2, "makeCopy" : false, "scalePoint" : qUnion([Q1])});
        }
    });
